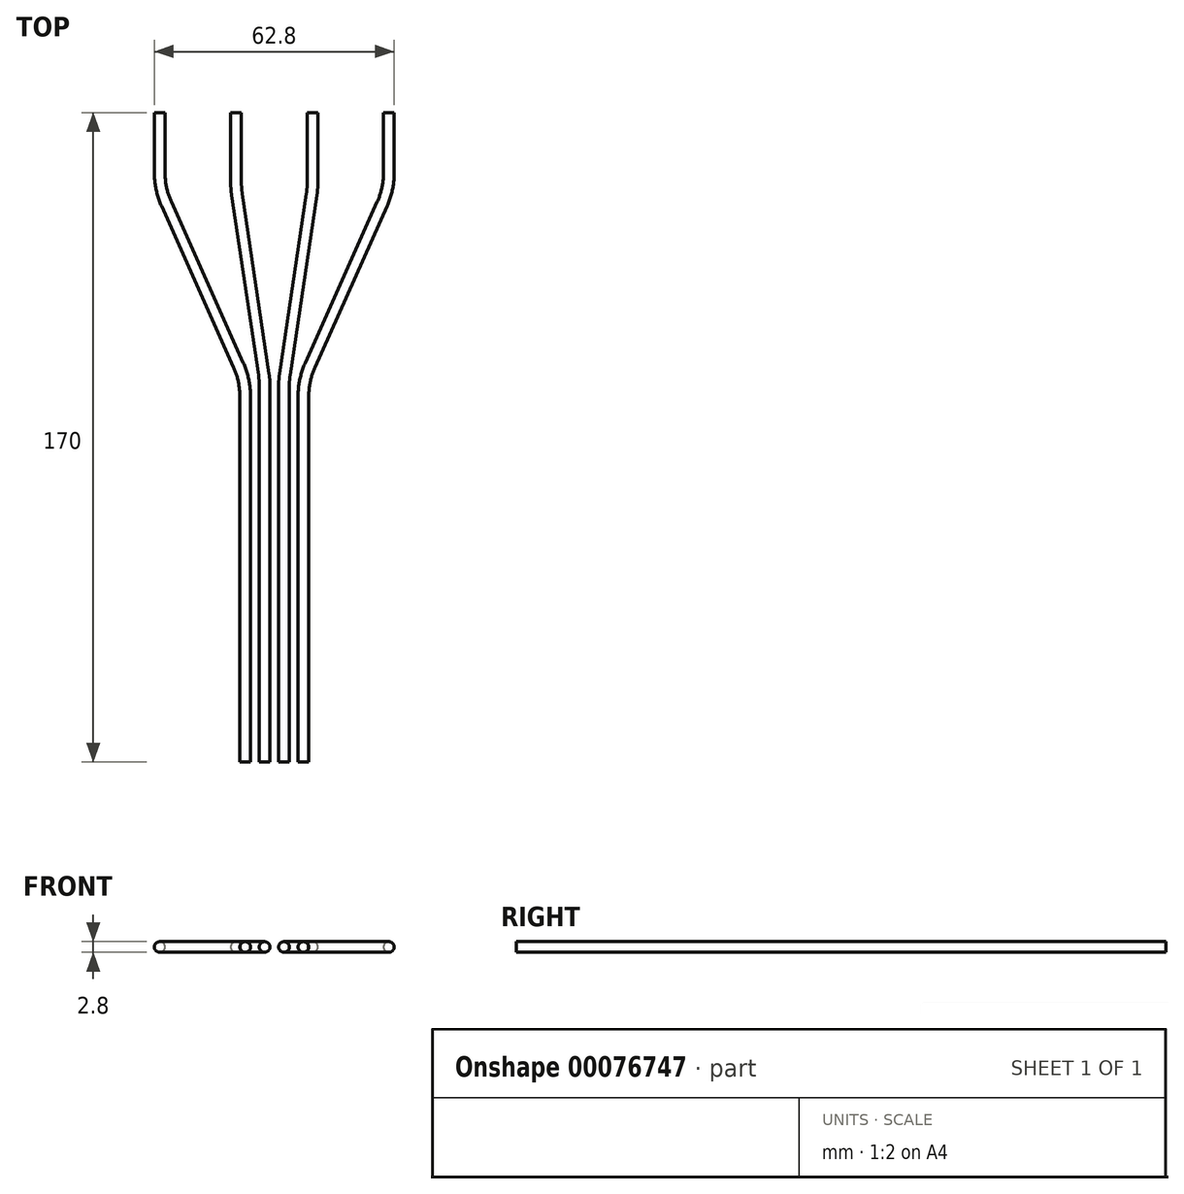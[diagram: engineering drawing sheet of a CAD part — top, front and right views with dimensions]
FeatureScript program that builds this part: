
annotation { "Feature Type Name" : "Feature", "Feature Type Description" : "" }
export const myFeature = defineFeature(function(context is Context, id is Id, definition is map)
    precondition{}
    {
        {
            var Q0;
            Q0=qCreatedBy(makeId("Top.planeOp"),FACE);
            var sketch = newSketch(context, id + "F0", { "sketchPlane" : qUnion([Q0])});
            skLineSegment(sketch, "E0", {"start": v(-7.62, 0) * mm, "end": v(-7.62, 95.73) * mm});
            skLineSegment(sketch, "E1", {"start": v(-9.37, 103.9) * mm, "end": v(-28.25, 146.1) * mm});
            skLineSegment(sketch, "E2", {"start": v(-30, 154.27) * mm, "end": v(-30, 170) * mm});
            skPoint(sketch, "E3.visualSharp", {"position": v(-7.62, 100) * mm});
            skArc(sketch, "E3.filletArc", {"start": v(-7.62, 95.73) * mm, "mid": v(-8.06, 99.9) * mm, "end": v(-9.37, 103.9) * mm});
            skPoint(sketch, "E4.visualSharp", {"position": v(-30, 150) * mm});
            skArc(sketch, "E4.filletArc", {"start": v(-30, 154.27) * mm, "mid": v(-29.56, 150.1) * mm, "end": v(-28.25, 146.1) * mm});
            skSolve(sketch);
        }
        {
            var Q0;
            Q0=qCreatedBy(makeId("Top.planeOp"),FACE);
            var sketch = newSketch(context, id + "F1", { "sketchPlane" : qUnion([Q0])});
            skLineSegment(sketch, "E5", {"start": v(-2.54, 0) * mm, "end": v(-2.54, 98.52) * mm});
            skLineSegment(sketch, "E6", {"start": v(-2.76, 101.47) * mm, "end": v(-9.78, 148.53) * mm});
            skLineSegment(sketch, "E7", {"start": v(-10, 151.48) * mm, "end": v(-10, 170) * mm});
            skPoint(sketch, "E8.visualSharp", {"position": v(-2.54, 100) * mm});
            skArc(sketch, "E8.filletArc", {"start": v(-2.54, 98.52) * mm, "mid": v(-2.6, 100) * mm, "end": v(-2.76, 101.47) * mm});
            skPoint(sketch, "E9.visualSharp", {"position": v(-10, 150) * mm});
            skArc(sketch, "E9.filletArc", {"start": v(-10, 151.48) * mm, "mid": v(-9.95, 150) * mm, "end": v(-9.78, 148.53) * mm});
            skSolve(sketch);
        }
        {
            var Q0;
            Q0=qCreatedBy(makeId("Top.planeOp"),FACE);
            var sketch = newSketch(context, id + "F2", { "sketchPlane" : qUnion([Q0])});
            skLineSegment(sketch, "E10", {"start": v(2.54, 0) * mm, "end": v(2.54, 98.52) * mm});
            skLineSegment(sketch, "E11", {"start": v(2.76, 101.47) * mm, "end": v(9.78, 148.53) * mm});
            skLineSegment(sketch, "E12", {"start": v(10, 151.48) * mm, "end": v(10, 170) * mm});
            skPoint(sketch, "E13.visualSharp", {"position": v(2.54, 100) * mm});
            skArc(sketch, "E13.filletArc", {"start": v(2.76, 101.47) * mm, "mid": v(2.6, 100) * mm, "end": v(2.54, 98.52) * mm});
            skPoint(sketch, "E14.visualSharp", {"position": v(10, 150) * mm});
            skArc(sketch, "E14.filletArc", {"start": v(9.78, 148.53) * mm, "mid": v(9.95, 150) * mm, "end": v(10, 151.48) * mm});
            skSolve(sketch);
        }
        {
            var Q0;
            Q0=qCreatedBy(makeId("Top.planeOp"),FACE);
            var sketch = newSketch(context, id + "F3", { "sketchPlane" : qUnion([Q0])});
            skLineSegment(sketch, "E15", {"start": v(7.62, 0) * mm, "end": v(7.62, 95.73) * mm});
            skLineSegment(sketch, "E16", {"start": v(9.37, 103.9) * mm, "end": v(28.25, 146.1) * mm});
            skLineSegment(sketch, "E17", {"start": v(30, 154.27) * mm, "end": v(30, 170) * mm});
            skPoint(sketch, "E18.visualSharp", {"position": v(7.62, 100) * mm});
            skArc(sketch, "E18.filletArc", {"start": v(9.37, 103.9) * mm, "mid": v(8.06, 99.9) * mm, "end": v(7.62, 95.73) * mm});
            skPoint(sketch, "E19.visualSharp", {"position": v(30, 150) * mm});
            skArc(sketch, "E19.filletArc", {"start": v(28.25, 146.1) * mm, "mid": v(29.56, 150.1) * mm, "end": v(30, 154.27) * mm});
            skSolve(sketch);
        }
        {
            var Q0;
            Q0=qCreatedBy(makeId("Front.planeOp"),FACE);
            var sketch = newSketch(context, id + "F4", { "sketchPlane" : qUnion([Q0])});
            skCircle(sketch, "E20", {"center": v(-7.62, 0) * mm, "radius": 1.4 * mm});
            skSolve(sketch);
        }
        {
            var Q0;
            Q0=qCreatedBy(makeId("Front.planeOp"),FACE);
            var sketch = newSketch(context, id + "F5", { "sketchPlane" : qUnion([Q0])});
            skCircle(sketch, "E21", {"center": v(-2.54, 0) * mm, "radius": 1.4 * mm});
            skSolve(sketch);
        }
        {
            var Q0;
            Q0=qCreatedBy(makeId("Front.planeOp"),FACE);
            var sketch = newSketch(context, id + "F6", { "sketchPlane" : qUnion([Q0])});
            skCircle(sketch, "E22", {"center": v(2.54, 0) * mm, "radius": 1.4 * mm});
            skSolve(sketch);
        }
        {
            var Q0;
            Q0=qCreatedBy(makeId("Front.planeOp"),FACE);
            var sketch = newSketch(context, id + "F7", { "sketchPlane" : qUnion([Q0])});
            skCircle(sketch, "E23", {"center": v(7.62, 0) * mm, "radius": 1.4 * mm});
            skSolve(sketch);
        }
        {
            var Q0;
            Q0=makeQuery(id+"F4.imprint","IMPRINT",FACE,{"disambiguationData":[TD([[makeQuery(id+"F4.imprint","IMPRINT",EDGE,{"derivedFrom":sQuery(id+"F4.wireOp",EDGE,"E20")}),1.0]])]});
            var Q1;
            Q1=qConstructionFilter(qBodyType(qCreatedBy(id+"F0",EDGE),BodyType.WIRE),ConstructionObject.NO);
            sweep(context, id + "F8", {"profiles" : qUnion([Q0]), "path" : qUnion([Q1])});
        }
        {
            var Q0;
            Q0=qSketchRegion(id+"F5",true);
            var Q1;
            Q1=qConstructionFilter(qBodyType(qCreatedBy(id+"F1",EDGE),BodyType.WIRE),ConstructionObject.NO);
            sweep(context, id + "F9", {"profiles" : qUnion([Q0]), "path" : qUnion([Q1])});
        }
        {
            var Q0;
            Q0=qSketchRegion(id+"F6",true);
            var Q1;
            Q1=qConstructionFilter(qBodyType(qCreatedBy(id+"F2",EDGE),BodyType.WIRE),ConstructionObject.NO);
            sweep(context, id + "F10", {"profiles" : qUnion([Q0]), "path" : qUnion([Q1])});
        }
        {
            var Q0;
            Q0=qSketchRegion(id+"F7",true);
            var Q1;
            Q1=qConstructionFilter(qBodyType(qCreatedBy(id+"F3",EDGE),BodyType.WIRE),ConstructionObject.NO);
            sweep(context, id + "F11", {"profiles" : qUnion([Q0]), "path" : qUnion([Q1])});
        }
    });
